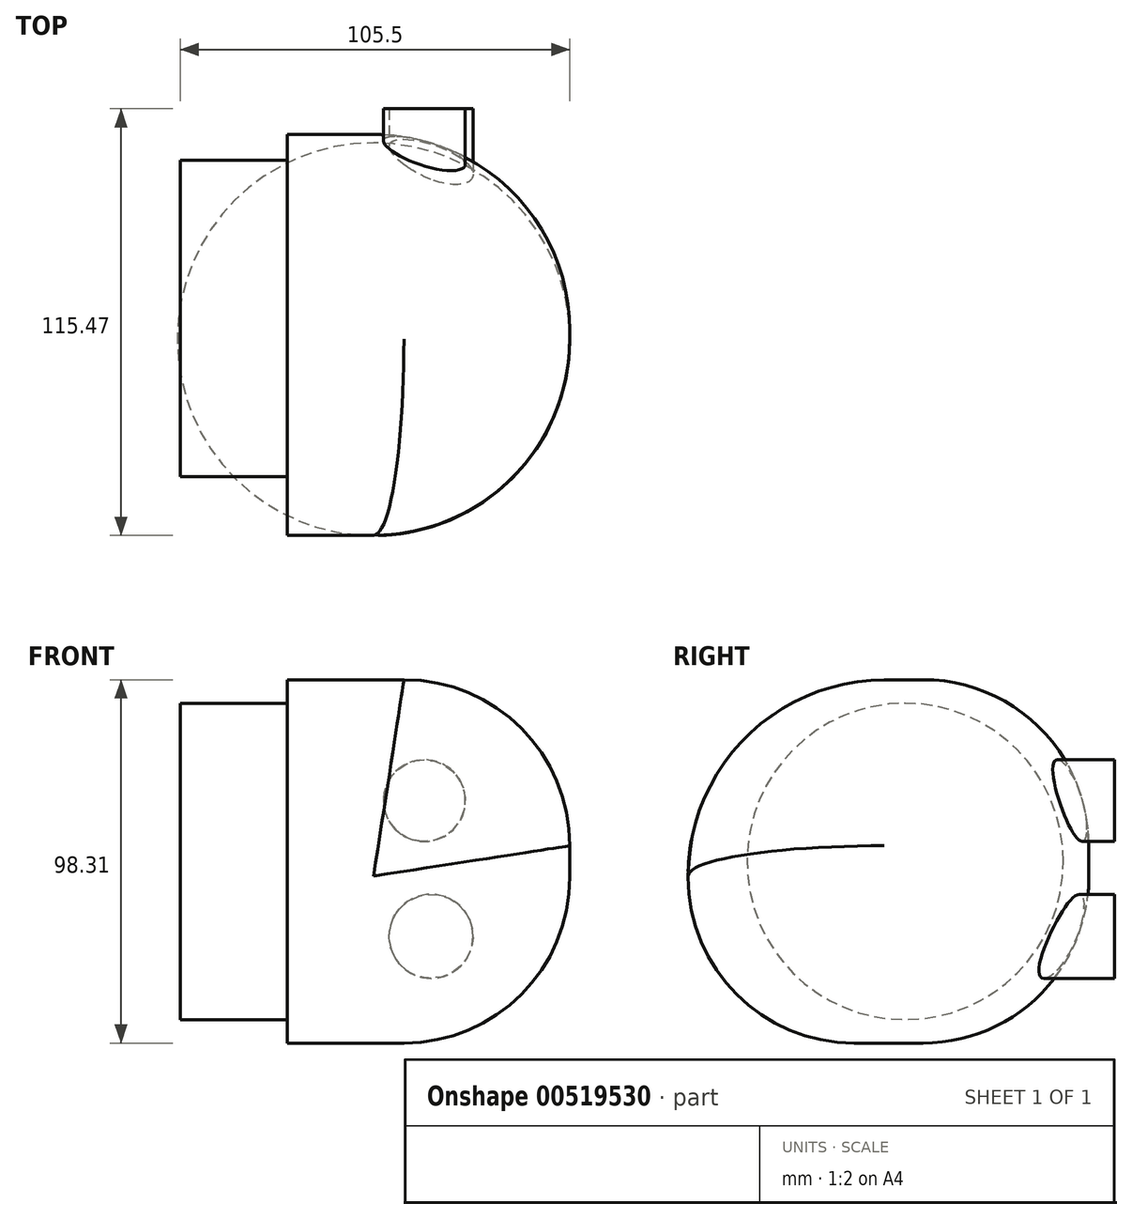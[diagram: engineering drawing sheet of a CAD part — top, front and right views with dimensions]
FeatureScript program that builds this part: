
annotation { "Feature Type Name" : "Feature", "Feature Type Description" : "" }
export const myFeature = defineFeature(function(context is Context, id is Id, definition is map)
    precondition{}
    {
        {
            var Q0;
            Q0=qCreatedBy(makeId("Right.planeOp"),FACE);
            var sketch = newSketch(context, id + "F0", { "sketchPlane" : qUnion([Q0])});
            skLineSegment(sketch, "E0.bottom", {"start": v(-93.27, 55.08) * mm, "end": v(15.22, 55.08) * mm});
            skLineSegment(sketch, "E0.top", {"start": v(-93.27, -43.23) * mm, "end": v(15.22, -43.23) * mm});
            skLineSegment(sketch, "E0.left", {"start": v(-93.27, 55.08) * mm, "end": v(-93.27, -43.23) * mm});
            skLineSegment(sketch, "E0.right", {"start": v(15.22, 55.08) * mm, "end": v(15.22, -43.23) * mm});
            skSolve(sketch);
        }
        {
            var Q0;
            Q0 = qSketchRegion(id + "F0", true);
            extrude(context, id + "F1", {"entities" : qUnion([Q0]), "depth" : 76.5 * mm, "offsetDistance" : 25 * mm});
        }
        {
            var Q0;
            Q0=makeQuery(id+"F1.opExtrude","SWEPT_EDGE",EDGE,{"disambiguationData":[OSD([sQuery(id+"F0.wireOp",EDGE,"E0.bottom"),sQuery(id+"F0.wireOp",EDGE,"E0.left")])]});
            var Q1;
            Q1=makeQuery(id+"F1.opExtrude","CAP_EDGE",EDGE,{"disambiguationData":[OSD([sQuery(id+"F0.wireOp",EDGE,"E0.right")])],"isStart":false});
            var Q2;
            Q2=makeQuery(id+"F1.opExtrude","CAP_EDGE",EDGE,{"disambiguationData":[OSD([sQuery(id+"F0.wireOp",EDGE,"E0.left")])],"isStart":false});
            fillet(context, id + "F2", {"entities" : qUnion([Q0, Q1, Q2]), "radius" : 53.1 * mm, "tangentPropagation" : true, "allowEdgeOverflow" : false});
        }
        {
            var Q0;
            Q0=makeQuery(id+"F2.opFillet","BLEND_FACE",FACE,{"disambiguationData":[OSD([sQuery(id+"F0.wireOp",EDGE,"E0.right")])]});
            fillet(context, id + "F3", {"entities" : qUnion([Q0]), "radius" : 44.9 * mm, "tangentPropagation" : true, "allowEdgeOverflow" : false});
        }
        {
            var Q0;
            Q0=qCreatedBy(makeId("Right.planeOp"),FACE);
            var sketch = newSketch(context, id + "F4", { "sketchPlane" : qUnion([Q0])});
            skCircle(sketch, "E1", {"center": v(-34.52, 5.9) * mm, "radius": 42.8 * mm});
            skSolve(sketch);
        }
        {
            var Q0;
            Q0 = qSketchRegion(id + "F4", true);
            extrude(context, id + "F5", {"entities" : qUnion([Q0]), "operationType" : NewBodyOperationType.ADD, "oppositeDirection" : true, "depth" : 29 * mm, "offsetDistance" : 25 * mm});
        }
        {
            var Q0;
            Q0=qCreatedBy(makeId("Front.planeOp"),FACE);
            var sketch = newSketch(context, id + "F6", { "sketchPlane" : qUnion([Q0])});
            skCircle(sketch, "E2", {"center": v(38.94, -14.34) * mm, "radius": 11.36 * mm});
            skCircle(sketch, "E3", {"center": v(37.14, 22.36) * mm, "radius": 11.05 * mm});
            skSolve(sketch);
        }
        {
            var Q0;
            Q0 = qSketchRegion(id + "F6", true);
            extrude(context, id + "F7", {"entities" : qUnion([Q0]), "operationType" : NewBodyOperationType.ADD, "oppositeDirection" : true, "depth" : 22.2 * mm, "offsetDistance" : 25 * mm});
        }
    });
